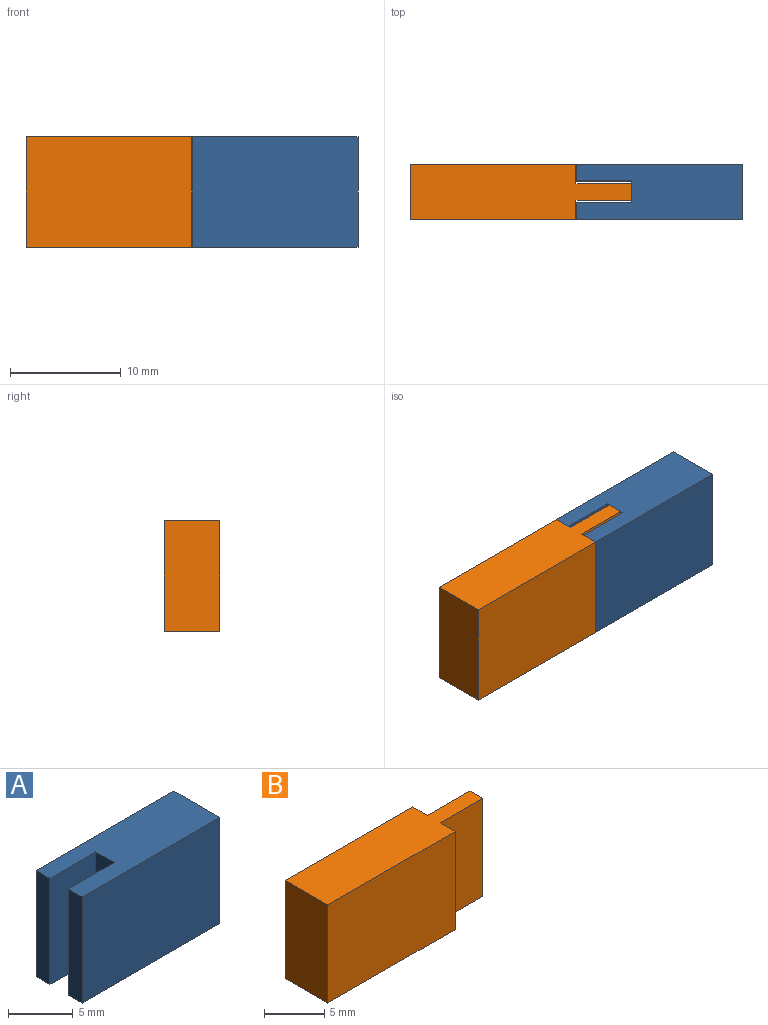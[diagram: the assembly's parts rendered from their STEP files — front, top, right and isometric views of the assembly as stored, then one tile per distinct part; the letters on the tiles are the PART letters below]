
ASSEMBLY  parts=2 mates=1
PART A: 10 faces, bbox 15x5x10 mm
  f0: plane 15x10mm, normal (0,1,0), area 150mm2, adj f1,f7,f8,f9
  f1: plane 10x1.5mm, normal (-1,0,0), area 15mm2, adj f0,f2,f8,f9
  f2: plane 10x5mm, normal (0,-1,0), area 50mm2, adj f1,f3,f8,f9
  f3: plane 10x2mm, normal (-1,0,0), area 20mm2, adj f2,f4,f8,f9
  f4: plane 10x5mm, normal (0,1,0), area 50mm2, adj f3,f5,f8,f9
  f5: plane 10x1.5mm, normal (-1,0,0), area 15mm2, adj f4,f6,f8,f9
  f6: plane 15x10mm, normal (0,-1,0), area 150mm2, adj f5,f7,f8,f9
  f7: plane 10x5mm, normal (1,0,0), area 50mm2, adj f0,f6,f8,f9
  f8: plane 15x5mm, normal (0,0,1), area 65mm2, adj f0,f1,f2,f3,f4,f5,f6,f7
  f9: plane 15x5mm, normal (0,0,-1), area 65mm2, adj f0,f1,f2,f3,f4,f5,f6,f7
PART B: 10 faces, bbox 20x5x10 mm
  f0: plane 10x1.75mm, normal (1,0,0), area 17.5mm2, adj f1,f7,f8,f9
  f1: plane 10x5mm, normal (0,-1,0), area 50mm2, adj f0,f2,f8,f9
  f2: plane 10x1.5mm, normal (1,0,0), area 15mm2, adj f1,f3,f8,f9
  f3: plane 10x5mm, normal (0,1,0), area 50mm2, adj f2,f4,f8,f9
  f4: plane 10x1.75mm, normal (1,0,0), area 17.5mm2, adj f3,f5,f8,f9
  f5: plane 15x10mm, normal (0,1,0), area 150mm2, adj f4,f6,f8,f9
  f6: plane 10x5mm, normal (-1,0,0), area 50mm2, adj f5,f7,f8,f9
  f7: plane 15x10mm, normal (0,-1,0), area 150mm2, adj f0,f6,f8,f9
  f8: plane 20x5mm, normal (0,0,1), area 82.5mm2, adj f0,f1,f2,f3,f4,f5,f6,f7
  f9: plane 20x5mm, normal (0,0,-1), area 82.5mm2, adj f0,f1,f2,f3,f4,f5,f6,f7
PLACE A t=(-2.5,0.75,0)mm
PLACE B t=(-2.5,0.75,0)mm
MATE planar A.f8 <-> B.f8  axis (0,0,1) through (-5,-1.75,10)mm
